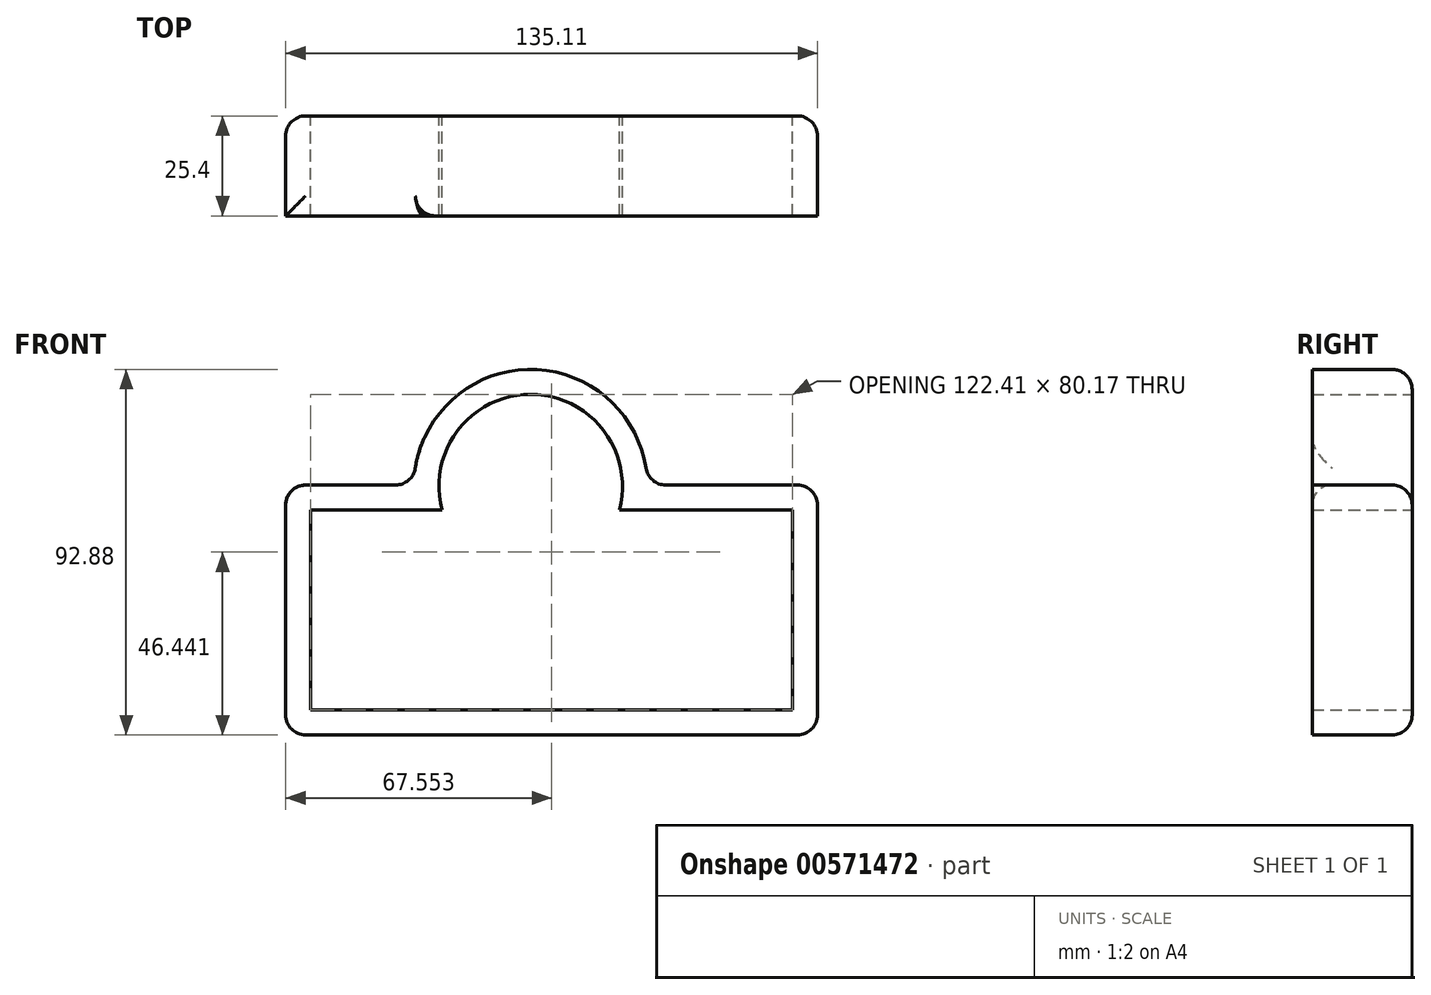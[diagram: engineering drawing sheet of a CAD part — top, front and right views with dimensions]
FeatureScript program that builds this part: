
annotation { "Feature Type Name" : "Feature", "Feature Type Description" : "" }
export const myFeature = defineFeature(function(context is Context, id is Id, definition is map)
    precondition{}
    {
        {
            var Q0;
            Q0=qCreatedBy(makeId("Front.planeOp"),FACE);
            var sketch = newSketch(context, id + "F0", { "sketchPlane" : qUnion([Q0])});
            skArc(sketch, "E0", {"start": v(22.52, -6.06) * mm, "mid": v(0, 23.32) * mm, "end": v(-22.52, -6.06) * mm});
            skLineSegment(sketch, "E1.bottom", {"start": v(-55.9, -6.06) * mm, "end": v(-22.52, -6.06) * mm});
            skLineSegment(sketch, "E1.top", {"start": v(-55.9, -56.86) * mm, "end": v(66.52, -56.86) * mm});
            skLineSegment(sketch, "E1.left", {"start": v(-55.9, -6.06) * mm, "end": v(-55.9, -56.86) * mm});
            skLineSegment(sketch, "E1.right", {"start": v(66.52, -6.06) * mm, "end": v(66.52, -56.86) * mm});
            skLineSegment(sketch, "E2.trimOffspring", {"start": v(22.52, -6.06) * mm, "end": v(66.52, -6.06) * mm});
            skLineSegment(sketch, "E3.0", {"start": v(29.67, 0.3) * mm, "end": v(72.87, 0.3) * mm});
            skLineSegment(sketch, "E3.1", {"start": v(-62.24, 0.3) * mm, "end": v(-29.67, 0.3) * mm});
            skLineSegment(sketch, "E3.2", {"start": v(-62.24, 0.3) * mm, "end": v(-62.24, -63.2) * mm});
            skArc(sketch, "E3.3", {"start": v(29.67, 0.3) * mm, "mid": v(0, 29.67) * mm, "end": v(-29.67, 0.3) * mm});
            skLineSegment(sketch, "E3.4", {"start": v(-62.24, -63.2) * mm, "end": v(72.87, -63.2) * mm});
            skLineSegment(sketch, "E3.5", {"start": v(72.87, 0.3) * mm, "end": v(72.87, -63.2) * mm});
            skSolve(sketch);
        }
        {
            var Q0;
            Q0=makeQuery(id+"F0.imprint","IMPRINT",FACE,{"disambiguationData":[TD([[makeQuery(id+"F0.imprint","IMPRINT",EDGE,{"derivedFrom":sQuery(id+"F0.wireOp",EDGE,"E0")}),-1.0]])]});
            extrude(context, id + "F1", {"entities" : qUnion([Q0]), "depth" : 25.4 * mm, "offsetDistance" : 25.4 * mm});
        }
        {
            var Q0;
            Q0=makeQuery(id+"F1.opExtrude","CAP_EDGE",EDGE,{"disambiguationData":[OSD([sQuery(id+"F0.wireOp",EDGE,"E3.0")])],"isStart":true});
            var Q1;
            Q1=makeQuery(id+"F1.opExtrude","CAP_EDGE",EDGE,{"disambiguationData":[OSD([sQuery(id+"F0.wireOp",EDGE,"E3.3")])],"isStart":true});
            var Q2;
            Q2=makeQuery(id+"F1.opExtrude","CAP_EDGE",EDGE,{"disambiguationData":[OSD([sQuery(id+"F0.wireOp",EDGE,"E3.1")])],"isStart":true});
            var Q3;
            Q3=makeQuery(id+"F1.opExtrude","CAP_EDGE",EDGE,{"disambiguationData":[OSD([sQuery(id+"F0.wireOp",EDGE,"E3.2")])],"isStart":true});
            var Q4;
            Q4=makeQuery(id+"F1.opExtrude","CAP_EDGE",EDGE,{"disambiguationData":[OSD([sQuery(id+"F0.wireOp",EDGE,"E3.4")])],"isStart":true});
            var Q5;
            Q5=makeQuery(id+"F1.opExtrude","CAP_EDGE",EDGE,{"disambiguationData":[OSD([sQuery(id+"F0.wireOp",EDGE,"E3.5")])],"isStart":true});
            var Q6;
            Q6=makeQuery(id+"F1.opExtrude","SWEPT_EDGE",EDGE,{"disambiguationData":[OSD([sQuery(id+"F0.wireOp",EDGE,"E3.0"),sQuery(id+"F0.wireOp",EDGE,"E3.5")])]});
            var Q7;
            Q7=makeQuery(id+"F1.opExtrude","SWEPT_EDGE",EDGE,{"disambiguationData":[OSD([sQuery(id+"F0.wireOp",EDGE,"E3.1"),sQuery(id+"F0.wireOp",EDGE,"E3.2")])]});
            var Q8;
            Q8=makeQuery(id+"F1.opExtrude","SWEPT_EDGE",EDGE,{"disambiguationData":[OSD([sQuery(id+"F0.wireOp",EDGE,"E3.0"),sQuery(id+"F0.wireOp",EDGE,"E3.3")])]});
            var Q9;
            Q9=makeQuery(id+"F1.opExtrude","SWEPT_FACE",FACE,{"disambiguationData":[OSD([sQuery(id+"F0.wireOp",EDGE,"E3.1")])]});
            var Q10;
            Q10=makeQuery(id+"F1.opExtrude","SWEPT_EDGE",EDGE,{"disambiguationData":[OSD([sQuery(id+"F0.wireOp",EDGE,"E3.2"),sQuery(id+"F0.wireOp",EDGE,"E3.4")])]});
            var Q11;
            Q11=makeQuery(id+"F1.opExtrude","SWEPT_EDGE",EDGE,{"disambiguationData":[OSD([sQuery(id+"F0.wireOp",EDGE,"E3.4"),sQuery(id+"F0.wireOp",EDGE,"E3.5")])]});
            fillet(context, id + "F2", {"entities" : qUnion([Q0, Q1, Q2, Q3, Q4, Q5, Q6, Q7, Q8, Q9, Q10, Q11]), "radius" : 5.08 * mm, "tangentPropagation" : true, "allowEdgeOverflow" : false});
        }
    });
